# Revit family: Domotics-DomesticRanges-GEWISS-CHORUS_CONTAINER-IP40
name_source: partatom
category: Apparecchi elettrici
revit_build: Autodesk Revit 2016 (Build: 20161004_0715(x64)
units: mm (PartAtom-declared; Revit-internal decimal feet)

## family parameters
Condiviso = Sì
Host = Superficie
Mantenere orientamento annotazione = Sì
Punto di calcolo locali = Sì
Quota connettore circolare = Usa diametro
Taglio con vuoti quando caricato = Sì
Tipo di parte = Normale

## types (1)
- Domotics-DomesticRanges-GEWISS-CHORUS_CONTAINER-IP40
    Altezza = 82 mm  [stored 0.269029 ft]
    Altezza foro = 45 mm  [stored 0.147638 ft]
    Catalogue = DOMOTICS
    Catalogue Range = CHORUS - BOXES
    Colour = Grey RAL 7035
    Description: = 4 gang
    Descrizione = PROTECTED CONTAINERS, 4-GANG IP40 GREY
    EAN code = 8011564279315
    Electrocod = 0212
    GW16503 - GW16504 = Sì
    Glow Wire Test = 650 °C
    Glow wire test: = 650 °C
    IDF = 45f05d24-7371-4ce0-86a3-8a78c14370a4
    IDT = f378d9c2-ff5e-4731-b089-f82dcb29959e
    IP degree = IP40
    Immagine tipo = GW16504.jpg
    Installation temperature = -25 +60 °C
    Insulation class = II
    Lid screws = Corrosion-resistant steel
    Lunghezza = 132 mm  [stored 0.433071 ft]
    Lunghezza foro = 92 mm  [stored 0.301837 ft]
    Material = Technopolymer
    Modello = GW16504
    No. knockout holes Ã˜23 = 8 on sides / 1 on the bottom
    Outer dim. LxHxD (mm) = 132x82x56
    Produttore = GEWISS S.p.A.
    Profondità = 56 mm
    Prospetto di default = 1219 mm
    SEO = Container
    Shock resistance = IK07
    Standard = EN 60670-1
    Standard; = EN 60670-1
    Technical sheet = https://www.gewiss.com
    Thermo-pressure with ball = 70
    Torque screws tightening = 0,8NM
    Type of knockout holes = Removable with tool
    URL = https://www.gewiss.com
    Version file RFA = 18.0

note: source unit labels omitted for Thermo-pressure with ball — the stored unit's dimension contradicts the parameter name (converter mislabeling)

note: [stored X ft] marks values corroborated as IEEE doubles in the binary element streams (Revit-internal decimal feet)
